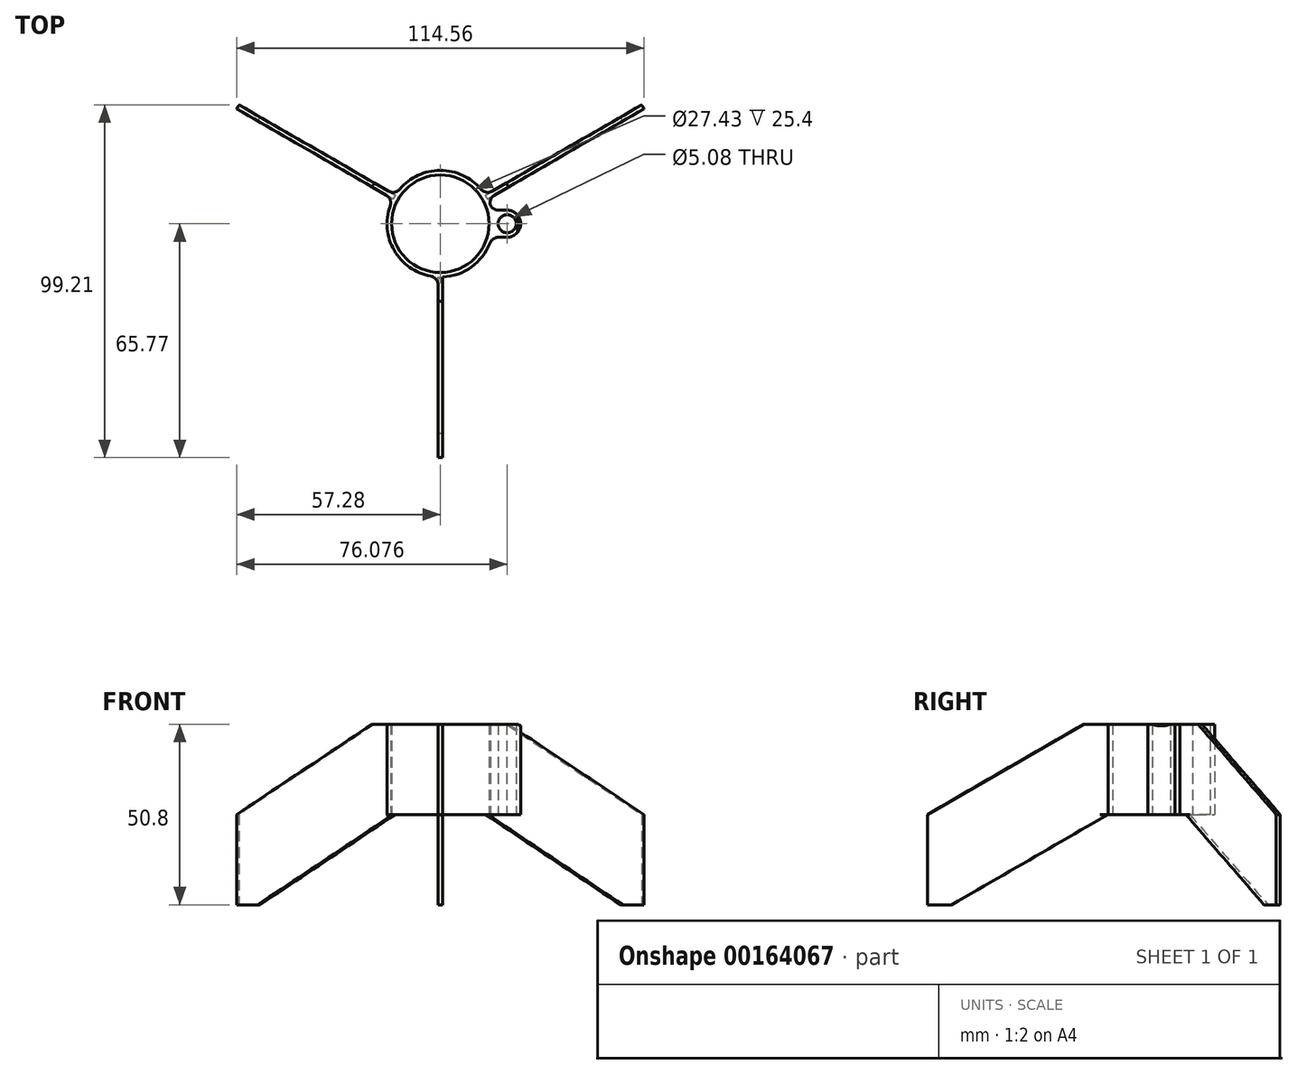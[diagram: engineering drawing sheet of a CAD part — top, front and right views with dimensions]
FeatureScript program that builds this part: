
annotation { "Feature Type Name" : "Feature", "Feature Type Description" : "" }
export const myFeature = defineFeature(function(context is Context, id is Id, definition is map)
    precondition{}
    {
        {
            var Q0;
            Q0=qCreatedBy(makeId("Top.planeOp"),FACE);
            var sketch = newSketch(context, id + "F0", { "sketchPlane" : qUnion([Q0])});
            skCircle(sketch, "E0", {"center": v(0, 0) * mm, "radius": 13.72 * mm});
            skCircle(sketch, "E1.0", {"center": v(0, 0) * mm, "radius": 14.99 * mm});
            skArc(sketch, "E2", {"start": v(18.76, -3.8) * mm, "mid": v(22.6, 0.07) * mm, "end": v(18.63, 3.8) * mm});
            skCircle(sketch, "E3.0", {"center": v(18.8, 0) * mm, "radius": 2.54 * mm});
            skLineSegment(sketch, "E4", {"start": v(18.63, 3.8) * mm, "end": v(14.5, 3.8) * mm});
            skLineSegment(sketch, "E5", {"start": v(18.76, -3.8) * mm, "end": v(14.5, -3.8) * mm});
            skLineSegment(sketch, "E6", {"start": v(0, 0) * mm, "end": v(0, -22.82) * mm, "construction": true});
            skLineSegment(sketch, "E7", {"start": v(0, 0) * mm, "end": v(21.34, 12.32) * mm, "construction": true});
            skLineSegment(sketch, "E8.MirrorCS", {"start": v(0, 0) * mm, "end": v(-21.34, 12.32) * mm, "construction": true});
            skLineSegment(sketch, "E9", {"start": v(13.28, 6.94) * mm, "end": v(57.28, 32.34) * mm});
            skLineSegment(sketch, "E10.MirrorCS", {"start": v(-13.28, 6.94) * mm, "end": v(-57.28, 32.34) * mm});
            skLineSegment(sketch, "E11.MirrorCS", {"start": v(12.65, 8.04) * mm, "end": v(56.64, 33.44) * mm});
            skLineSegment(sketch, "E12.MirrorCS", {"start": v(-12.65, 8.04) * mm, "end": v(-56.64, 33.44) * mm});
            skLineSegment(sketch, "E13", {"start": v(0.63, -14.97) * mm, "end": v(0.63, -65.77) * mm});
            skLineSegment(sketch, "E14.MirrorCS", {"start": v(-0.63, -14.97) * mm, "end": v(-0.63, -65.77) * mm});
            skLineSegment(sketch, "E15", {"start": v(0.63, -65.77) * mm, "end": v(-0.63, -65.77) * mm});
            skLineSegment(sketch, "E16", {"start": v(57.28, 32.34) * mm, "end": v(56.64, 33.44) * mm});
            skLineSegment(sketch, "E17", {"start": v(-56.64, 33.44) * mm, "end": v(-57.28, 32.34) * mm});
            skSolve(sketch);
        }
        {
            var Q0;
            Q0=makeQuery(id+"F0.imprint","IMPRINT",FACE,{"disambiguationData":[TD([[makeQuery(id+"F0.imprint","IMPRINT",EDGE,{"derivedFrom":sQuery(id+"F0.wireOp",EDGE,"E0")}),-1.0]])]});
            var Q1;
            Q1=makeQuery(id+"F0.imprint","IMPRINT",FACE,{"disambiguationData":[TD([[makeQuery(id+"F0.imprint","IMPRINT",EDGE,{"derivedFrom":sQuery(id+"F0.wireOp",EDGE,"E3.0")}),-1.0]])]});
            extrude(context, id + "F1", {"entities" : qUnion([Q0, Q1]), "depth" : 25.4 * mm, "offsetDistance" : 25.4 * mm});
        }
        {
            var Q0;
            {var subQ0=sQuery(id+"F0.wireOp",EDGE,"E10.MirrorCS");Q0=makeQuery(id+"F0.imprint","IMPRINT",FACE,{"disambiguationData":[TD([[makeQuery(id+"F0.imprint","IMPRINT",EDGE,{"derivedFrom":subQ0}),-1.0]])]});}
            var Q1;
            {var subQ0=sQuery(id+"F0.wireOp",EDGE,"E9");Q1=makeQuery(id+"F0.imprint","IMPRINT",FACE,{"disambiguationData":[TD([[makeQuery(id+"F0.imprint","IMPRINT",EDGE,{"derivedFrom":subQ0}),1.0]])]});}
            var Q2;
            {var subQ0=sQuery(id+"F0.wireOp",EDGE,"E13");Q2=makeQuery(id+"F0.imprint","IMPRINT",FACE,{"disambiguationData":[TD([[makeQuery(id+"F0.imprint","IMPRINT",EDGE,{"derivedFrom":subQ0}),-1.0]])]});}
            extrude(context, id + "F2", {"entities" : qUnion([Q0, Q1, Q2]), "operationType" : NewBodyOperationType.ADD, "endBound" : BoundingType.SYMMETRIC, "depth" : 50.8 * mm, "offsetDistance" : 25.4 * mm});
        }
        {
            var Q0;
            Q0=qCreatedBy(makeId("Right.planeOp"),FACE);
            var sketch = newSketch(context, id + "F3", { "sketchPlane" : qUnion([Q0])});
            skLineSegment(sketch, "E18", {"start": v(0, 0) * mm, "end": v(0, 81) * mm, "construction": true});
            skLineSegment(sketch, "E19.0", {"start": v(-14.97, 25.4) * mm, "end": v(-65.77, 25.4) * mm});
            skLineSegment(sketch, "E20.0", {"start": v(-65.77, 25.4) * mm, "end": v(-65.77, 0) * mm});
            skLineSegment(sketch, "E21.0", {"start": v(-14.97, -25.4) * mm, "end": v(-58.97, -25.4) * mm});
            skLineSegment(sketch, "E22.0", {"start": v(-14.97, 0) * mm, "end": v(-14.97, -25.4) * mm});
            skLineSegment(sketch, "E23", {"start": v(-21.78, 25.4) * mm, "end": v(-65.77, 0) * mm});
            skLineSegment(sketch, "E24", {"start": v(-14.97, 0) * mm, "end": v(-58.97, -25.4) * mm});
            skPoint(sketch, "E25.orphan", {"position": v(-65.77, -25.4) * mm});
            skSolve(sketch);
        }
        {
            var Q0;
            Q0 = qSketchRegion(id + "F3", true);
            var Q1;
            Q1=sQuery(id+"F3.wireOp",EDGE,"E18");
            revolve(context, id + "F4", {"operationType" : NewBodyOperationType.REMOVE, "surfaceOperationType" : NewSurfaceOperationType.NEW, "entities" : qUnion([Q0]), "axis" : qUnion([Q1]), "revolveType" : RevolveType.FULL, "oppositeDirection" : true});
        }
        {
            var Q0;
            {var subQ0=sQuery(id+"F0.wireOp",EDGE,"E1.0");var subQ1=sQuery(id+"F0.wireOp",EDGE,"E12.MirrorCS");Q0=makeQuery(id+"F2.boolean.opBoolean","SPLIT",EDGE,{"disambiguationData":[topologyDisambiguationEdgeConnected([makeQuery(id+"F1.opExtrude","SWEPT_FACE",FACE,{"disambiguationData":[OSD([subQ0])]})])],"derivedFrom":makeQuery(id+"F2.opExtrude","SWEPT_EDGE",EDGE,{"disambiguationData":[OSD([subQ0,subQ1])]})});}
            var Q1;
            {var subQ0=sQuery(id+"F0.wireOp",EDGE,"E1.0");var subQ1=sQuery(id+"F0.wireOp",EDGE,"E11.MirrorCS");Q1=makeQuery(id+"F2.boolean.opBoolean","SPLIT",EDGE,{"disambiguationData":[topologyDisambiguationEdgeConnected([makeQuery(id+"F1.opExtrude","SWEPT_FACE",FACE,{"disambiguationData":[OSD([subQ0])]})])],"derivedFrom":makeQuery(id+"F2.opExtrude","SWEPT_EDGE",EDGE,{"disambiguationData":[OSD([subQ0,subQ1])]})});}
            var Q2;
            {var subQ0=sQuery(id+"F0.wireOp",EDGE,"E1.0");var subQ1=sQuery(id+"F0.wireOp",EDGE,"E10.MirrorCS");Q2=makeQuery(id+"F2.boolean.opBoolean","SPLIT",EDGE,{"disambiguationData":[topologyDisambiguationEdgeConnected([makeQuery(id+"F1.opExtrude","SWEPT_FACE",FACE,{"disambiguationData":[OSD([subQ0])]})])],"derivedFrom":makeQuery(id+"F2.opExtrude","SWEPT_EDGE",EDGE,{"disambiguationData":[OSD([subQ0,subQ1])]})});}
            var Q3;
            {var subQ0=sQuery(id+"F0.wireOp",EDGE,"E1.0");var subQ1=sQuery(id+"F0.wireOp",EDGE,"E14.MirrorCS");Q3=makeQuery(id+"F2.boolean.opBoolean","SPLIT",EDGE,{"disambiguationData":[topologyDisambiguationEdgeConnected([makeQuery(id+"F1.opExtrude","SWEPT_FACE",FACE,{"disambiguationData":[OSD([subQ0])]})])],"derivedFrom":makeQuery(id+"F2.opExtrude","SWEPT_EDGE",EDGE,{"disambiguationData":[OSD([subQ0,subQ1])]})});}
            var Q4;
            {var subQ0=sQuery(id+"F0.wireOp",EDGE,"E1.0");var subQ1=sQuery(id+"F0.wireOp",EDGE,"E13");Q4=makeQuery(id+"F2.boolean.opBoolean","SPLIT",EDGE,{"disambiguationData":[topologyDisambiguationEdgeConnected([makeQuery(id+"F1.opExtrude","SWEPT_FACE",FACE,{"disambiguationData":[OSD([subQ0])]})])],"derivedFrom":makeQuery(id+"F2.opExtrude","SWEPT_EDGE",EDGE,{"disambiguationData":[OSD([subQ0,subQ1])]})});}
            var Q5;
            {var subQ0=sQuery(id+"F0.wireOp",EDGE,"E1.0");var subQ1=sQuery(id+"F0.wireOp",EDGE,"E9");Q5=makeQuery(id+"F2.boolean.opBoolean","SPLIT",EDGE,{"disambiguationData":[topologyDisambiguationEdgeConnected([makeQuery(id+"F1.opExtrude","SWEPT_FACE",FACE,{"disambiguationData":[OSD([subQ0])]})])],"derivedFrom":makeQuery(id+"F2.opExtrude","SWEPT_EDGE",EDGE,{"disambiguationData":[OSD([subQ0,subQ1])]})});}
            var Q6;
            Q6=makeQuery(id+"F1.opExtrude","SWEPT_EDGE",EDGE,{"disambiguationData":[OSD([sQuery(id+"F0.wireOp",EDGE,"E1.0"),sQuery(id+"F0.wireOp",EDGE,"E5")])]});
            var Q7;
            Q7=makeQuery(id+"F1.opExtrude","SWEPT_EDGE",EDGE,{"disambiguationData":[OSD([sQuery(id+"F0.wireOp",EDGE,"E1.0"),sQuery(id+"F0.wireOp",EDGE,"E4")])]});
            fillet(context, id + "F5", {"entities" : qUnion([Q0, Q1, Q2, Q3, Q4, Q5, Q6, Q7]), "radius" : 2.54 * mm, "tangentPropagation" : true, "defaultsChanged" : false, "vertexSettings" : [], "allowEdgeOverflow" : false});
        }
    });
